# Revit family: Profilhalter
name_source: partatom
category: HLS-Bauteile
revit_build: Autodesk Revit 2017 (Build: 20190507_1515(x64)
units: mm (PartAtom-declared; Revit-internal decimal feet)

## family parameters
Arbeitsebenenbasiert = Ja
Beim Laden mit Abzugskörper schneiden = Nein
Bemaßung runder Anschluss = Durchmesser verwenden
Gemeinsam genutzt = Ja
Immer vertikal = Nein
Raumberechnungspunkt = Nein
Teiletyp = Normal

## types (1)
- Profilhalter 27
    Artikelnummer = 0809504
    D = 11 mm
    Fabrikat = MEFA
    Firma = MEFA Befestigungs- und Montagesysteme GmbH
    Gewicht = 0.01 kg
    Gewicht pro Bauteil = 0.01 kg
    H = 8 mm  [stored 0.0262467 ft]
    Höhe = 8 mm
    Kurztext1 = Profilhalter C-Profil 27
    Kurztext2 = Bohrung 10.5 mm für Gewinde M10
    L = 28 mm  [stored 0.0918635 ft]
    Lochdurchmesser = 10.5 mm
    Länge = 32 mm  [stored 0.104987 ft]
    Material = Stahl
    Materialname = S235
    Mengeneinheit = St
    Oberflaeche = galvanisch verzinkt
    Profiltyp = 27
    Stärke Material = 2 mm  [stored 0.00656168 ft]
    Vorgabe-Ansicht = 1219 mm
    max. zul. Last = 0.00 kN
    vpe = 100 St

note: [stored X ft] marks values corroborated as IEEE doubles in the binary element streams (Revit-internal decimal feet)
